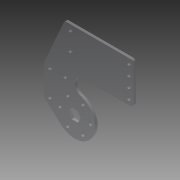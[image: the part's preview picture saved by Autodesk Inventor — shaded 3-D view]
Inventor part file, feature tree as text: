
AUTODESK INVENTOR PART (.ipt)
format: ipt  version: 2014 (Build 180170000, 170)  size: 167,424 bytes
history: native  units: in
note: dims shown in document units (in); Inventor stores cm internally (conversion verified against a paired STEP export)
features: extrude x2, fillet x1, sketch x1
ambient origin geometry x8: Origin, YZ Plane, XZ Plane, XY Plane, X Axis, Y Axis, Z Axis, Center Point
bodies: Solid1 (feature_tree)
feature tree (4):
  extrude  "Extrusion1"  Depth=0.125in
  extrude  "Extrusion2"  Depth=0.5in
  fillet  "Fillet2"  Radius=0.164in
  sketch  "Sketch2"  dims[d3=0.125in d4=0.0in d7=0.625in d8=0.5in d23=0.164in d25=0.75in d26=0.0in d27=2.3622in d29=360.0deg d41=2.0in d42=0.75in d43=0.75in d44=1.5in d55=2.875in d57=0.164in d58=0.25in d59=0.25in d60=1.5748in d62=0.5in d63=0.3937in d65=1.0in d67=0.25in d68=1.444in d69=2.0in d70=1.5in d71=0.7833in d72=2.25in d76=2.2202in d78=0.25in d79=0.375in d82=0.7874in d84=0.75in d85=0.3937in d87=1.0in d91=1.25in d96=0.7874in d98=1.0in d99=0.3937in d101=1.0in d103=0.7874in d105=0.875in d106=0.3937in d108=1.0in d110=1.0in d111=1.0in d112=0.0in d113=0.25in d114=0.125in]
